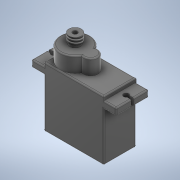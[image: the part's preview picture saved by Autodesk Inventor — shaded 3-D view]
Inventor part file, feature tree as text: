
AUTODESK INVENTOR PART (.ipt)
format: ipt  version: 2020 (Build 240168000, 168)  size: 270,336 bytes
history: native  units: mm
features: extrude x7, sketch x7, thread x2, fillet x1
ambient origin geometry x8: Origin, YZ Plane, XZ Plane, XY Plane, X Axis, Y Axis, Z Axis, Center Point
bodies: Solid1 (feature_tree)
feature tree (17):
  extrude  "Extrusion1"  Depth=22.7mm
  extrude  "Extrusion2"  Depth=4.7mm
  extrude  "Extrusion3"  Depth=2.7mm TaperAngle=0.0deg
  extrude  "Extrusion4"  Depth=12.3mm TaperAngle=0.0deg
  extrude  "Extrusion5"  Depth=5.7mm
  extrude  "Extrusion6"  Depth=5.4mm
  extrude  "Extrusion7"  Depth=0.5mm TaperAngle=0.0deg
  thread  "Thread1"  [1 undecoded]
  thread  "Thread2"  [1 undecoded]
  fillet  "Fillet1"  Radius=4.7mm
  sketch  "Sketch1"  dims[d0=22.7mm d1=22.7mm]
  sketch  "Sketch2"  dims[d2=1.5mm d3=4.7mm]
  sketch  "Sketch3"  dims[d4=2.7mm d5=12.3mm d6=0.0mm]
  sketch  "Sketch4"  dims[d7=2.0mm d10=12.3mm d11=0.0mm]
  sketch  "Sketch5"  dims[d12=11.4mm d13=5.7mm]
  sketch  "Sketch6"  dims[d15=12.3mm d16=5.4mm]
  sketch  "Sketch7"  dims[d17=14.3mm d18=5.7mm d19=0.0mm d20=4.0mm d21=1.0mm d22=0.0mm d23=4.7mm d24=2.7mm d25=0.0mm d26=1.8mm d27=0.3mm d28=0.0mm d29=1.5mm d30=2.0mm d31=0.0mm d32=2.0mm d33=0.0mm d34=2.7mm d35=0.0mm d36=0.5mm]
note: 2 required parameter values undecoded (feature->parameter linkage not recoverable at this tier; creation-order binding heuristic only, values carry confidence <= 0.55)
